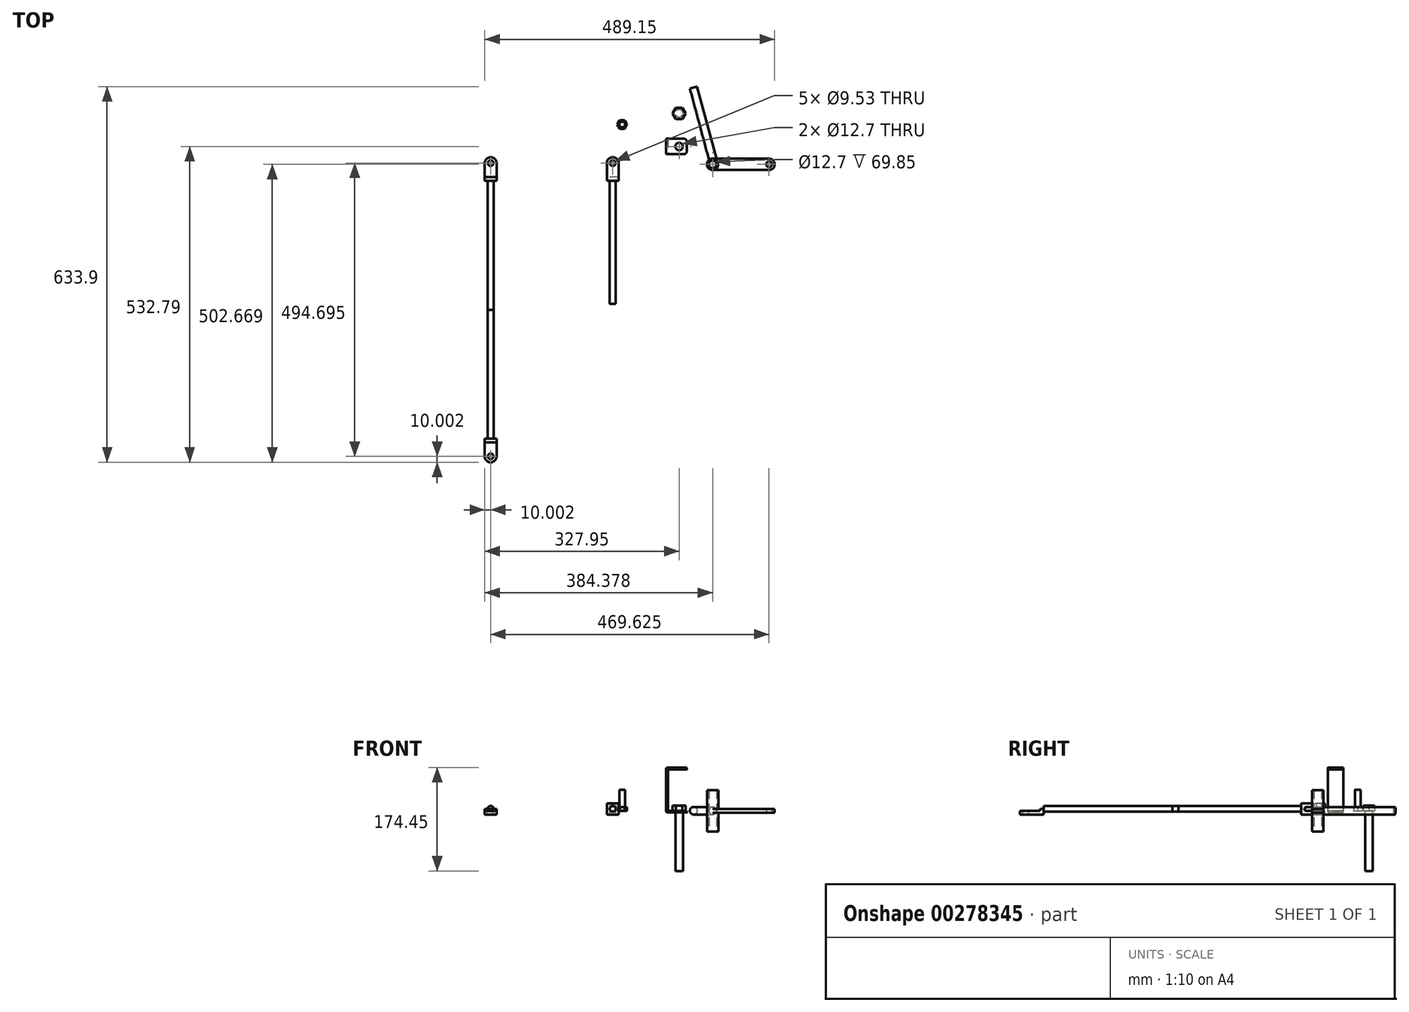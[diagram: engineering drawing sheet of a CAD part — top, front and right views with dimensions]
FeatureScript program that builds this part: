
annotation { "Feature Type Name" : "Feature", "Feature Type Description" : "" }
export const myFeature = defineFeature(function(context is Context, id is Id, definition is map)
    precondition{}
    {
        {
            var Q0;
            Q0=qCreatedBy(makeId("Top.planeOp"),FACE);
            var sketch = newSketch(context, id + "F0", { "sketchPlane" : qUnion([Q0])});
            skCircle(sketch, "E0", {"center": v(0, 0) * mm, "radius": 6.35 * mm});
            skLineSegment(sketch, "E1.bottom", {"start": v(8, 13) * mm, "end": v(-22, 13) * mm});
            skLineSegment(sketch, "E1.top", {"start": v(8, -13) * mm, "end": v(-22, -13) * mm});
            skLineSegment(sketch, "E1.left", {"start": v(13, 8) * mm, "end": v(13, -8) * mm});
            skLineSegment(sketch, "E1.right", {"start": v(-22, 13) * mm, "end": v(-22, -13) * mm});
            skLineSegment(sketch, "E2", {"start": v(-19, 13) * mm, "end": v(-19, -13) * mm});
            skPoint(sketch, "E3.visualSharp", {"position": v(13, 13) * mm});
            skArc(sketch, "E3.filletArc", {"start": v(13, 8) * mm, "mid": v(11.54, 11.54) * mm, "end": v(8, 13) * mm});
            skPoint(sketch, "E4.visualSharp", {"position": v(13, -13) * mm});
            skArc(sketch, "E4.filletArc", {"start": v(8, -13) * mm, "mid": v(11.54, -11.54) * mm, "end": v(13, -8) * mm});
            skSolve(sketch);
        }
        {
            var Q0;
            Q0=makeQuery(id+"F0.imprint","IMPRINT",FACE,{"disambiguationData":[TD([[makeQuery(id+"F0.imprint","IMPRINT",EDGE,{"derivedFrom":sQuery(id+"F0.wireOp",EDGE,"E0")}),-1.0]])]});
            var Q1;
            {var subQ0=sQuery(id+"F0.wireOp",EDGE,"E1.right");Q1=makeQuery(id+"F0.imprint","IMPRINT",FACE,{"disambiguationData":[TD([[makeQuery(id+"F0.imprint","IMPRINT",EDGE,{"derivedFrom":subQ0}),1.0]])]});}
            extrude(context, id + "F1", {"entities" : qUnion([Q0, Q1]), "oppositeDirection" : true, "depth" : 3 * mm});
        }
        {
            var Q0;
            {var subQ0=sQuery(id+"F0.wireOp",EDGE,"E1.right");Q0=makeQuery(id+"F0.imprint","IMPRINT",FACE,{"disambiguationData":[TD([[makeQuery(id+"F0.imprint","IMPRINT",EDGE,{"derivedFrom":subQ0}),1.0]])]});}
            extrude(context, id + "F2", {"entities" : qUnion([Q0]), "operationType" : NewBodyOperationType.ADD, "depth" : 34.92 * mm});
        }
        {
            var Q0;
            Q0=makeQuery(id+"F1.opExtrude","SWEPT_BODY",BODY,{"disambiguationData":[OSD([sQuery(id+"F0.wireOp",EDGE,"E0"),sQuery(id+"F0.wireOp",EDGE,"E1.bottom"),sQuery(id+"F0.wireOp",EDGE,"E1.top"),sQuery(id+"F0.wireOp",EDGE,"E1.left"),sQuery(id+"F0.wireOp",EDGE,"E1.right")])]});
            var Q1;
            Q1=makeQuery(id+"F2.opExtrude","CAP_FACE",FACE,{"disambiguationData":[OSD([sQuery(id+"F0.wireOp",EDGE,"E1.bottom"),sQuery(id+"F0.wireOp",EDGE,"E1.top"),sQuery(id+"F0.wireOp",EDGE,"E1.right"),sQuery(id+"F0.wireOp",EDGE,"E2")])],"isStart":false});
            mirror(context, id + "F3", {"operationType" : NewBodyOperationType.ADD, "entities" : qUnion([Q0]), "mirrorPlane" : qUnion([Q1])});
        }
        {
            var Q0;
            Q0=qCreatedBy(makeId("Top.planeOp"),FACE);
            var sketch = newSketch(context, id + "F4", { "sketchPlane" : qUnion([Q0])});
            skCircle(sketch, "E5.cCircle", {"center": v(0, 56.05) * mm, "radius": 9.53 * mm, "construction": true});
            skLineSegment(sketch, "E5.0", {"start": v(-5.5, 65.57) * mm, "end": v(5.5, 65.57) * mm});
            skLineSegment(sketch, "E5.1", {"start": v(5.5, 65.57) * mm, "end": v(11, 56.05) * mm});
            skLineSegment(sketch, "E5.2", {"start": v(11, 56.05) * mm, "end": v(5.5, 46.52) * mm});
            skLineSegment(sketch, "E5.3", {"start": v(5.5, 46.52) * mm, "end": v(-5.5, 46.52) * mm});
            skLineSegment(sketch, "E5.4", {"start": v(-5.5, 46.52) * mm, "end": v(-11, 56.05) * mm});
            skLineSegment(sketch, "E5.5", {"start": v(-11, 56.05) * mm, "end": v(-5.5, 65.57) * mm});
            skPoint(sketch, "E5.0.midPoint", {"position": v(0, 65.57) * mm});
            skSolve(sketch);
        }
        {
            var Q0;
            Q0=makeQuery(id+"F4.imprint","IMPRINT",FACE,{"disambiguationData":[TD([[makeQuery(id+"F4.imprint","IMPRINT",EDGE,{"derivedFrom":sQuery(id+"F4.wireOp",EDGE,"E5.0")}),-1.0]])]});
            extrude(context, id + "F5", {"entities" : qUnion([Q0]), "depth" : 8.73 * mm});
        }
        {
            var Q0;
            Q0=makeQuery(id+"F5.opExtrude","CAP_FACE",FACE,{"disambiguationData":[OSD([sQuery(id+"F4.wireOp",EDGE,"E5.0"),sQuery(id+"F4.wireOp",EDGE,"E5.1"),sQuery(id+"F4.wireOp",EDGE,"E5.2"),sQuery(id+"F4.wireOp",EDGE,"E5.3"),sQuery(id+"F4.wireOp",EDGE,"E5.4"),sQuery(id+"F4.wireOp",EDGE,"E5.5")])],"isStart":true});
            var sketch = newSketch(context, id + "F6", { "sketchPlane" : qUnion([Q0])});
            skLineSegment(sketch, "E6", {"start": v(11, -56.05) * mm, "end": v(-11, -56.05) * mm, "construction": true});
            skLineSegment(sketch, "E7", {"start": v(0, -65.57) * mm, "end": v(0, -46.52) * mm, "construction": true});
            skCircle(sketch, "E8", {"center": v(0, -56.05) * mm, "radius": 6.35 * mm});
            skSolve(sketch);
        }
        {
            var Q0;
            Q0=makeQuery(id+"F6.imprint","IMPRINT",FACE,{"disambiguationData":[TD([[makeQuery(id+"F6.imprint","IMPRINT",EDGE,{"derivedFrom":sQuery(id+"F6.wireOp",EDGE,"E8")}),1.0]])]});
            extrude(context, id + "F7", {"entities" : qUnion([Q0]), "operationType" : NewBodyOperationType.ADD, "depth" : 101.6 * mm});
        }
        {
            var Q0;
            Q0=qCreatedBy(makeId("Top.planeOp"),FACE);
            var sketch = newSketch(context, id + "F8", { "sketchPlane" : qUnion([Q0])});
            skCircle(sketch, "E9", {"center": v(56.43, -30.12) * mm, "radius": 6.35 * mm});
            skCircle(sketch, "E10", {"center": v(56.43, -30.12) * mm, "radius": 9.53 * mm});
            skLineSegment(sketch, "E11", {"start": v(161.2, -30.12) * mm, "end": v(161.2, -30.12) * mm});
            skLineSegment(sketch, "E12", {"start": v(56.43, -20.6) * mm, "end": v(56.43, -39.65) * mm, "construction": true});
            skLineSegment(sketch, "E13", {"start": v(151.68, -20.6) * mm, "end": v(56.43, -20.6) * mm});
            skLineSegment(sketch, "E14", {"start": v(56.43, -39.65) * mm, "end": v(151.68, -39.65) * mm});
            skLineSegment(sketch, "E15", {"start": v(161.2, -30.12) * mm, "end": v(56.43, -30.12) * mm, "construction": true});
            skPoint(sketch, "E16.visualSharp", {"position": v(161.2, -20.6) * mm});
            skArc(sketch, "E16.filletArc", {"start": v(161.2, -30.12) * mm, "mid": v(158.41, -23.39) * mm, "end": v(151.68, -20.6) * mm});
            skPoint(sketch, "E17.visualSharp", {"position": v(161.2, -39.65) * mm});
            skArc(sketch, "E17.filletArc", {"start": v(151.68, -39.65) * mm, "mid": v(158.41, -36.86) * mm, "end": v(161.2, -30.12) * mm});
            skCircle(sketch, "E18", {"center": v(151.68, -30.12) * mm, "radius": 4.76 * mm});
            skLineSegment(sketch, "E19", {"start": v(56.43, -20.6) * mm, "end": v(24.26, 99.47) * mm, "construction": true});
            skLineSegment(sketch, "E20", {"start": v(24.26, 99.47) * mm, "end": v(18.12, 97.83) * mm});
            skLineSegment(sketch, "E21", {"start": v(24.26, 99.47) * mm, "end": v(30.4, 101.11) * mm});
            skLineSegment(sketch, "E22", {"start": v(30.4, 101.11) * mm, "end": v(63, -20.6) * mm});
            skLineSegment(sketch, "E23", {"start": v(18.12, 97.83) * mm, "end": v(50.42, -22.73) * mm});
            skSolve(sketch);
        }
        {
            var Q0;
            Q0=makeQuery(id+"F8.imprint","IMPRINT",FACE,{"disambiguationData":[TD([[makeQuery(id+"F8.imprint","IMPRINT",EDGE,{"derivedFrom":sQuery(id+"F8.wireOp",EDGE,"E9")}),-1.0]])]});
            extrude(context, id + "F9", {"entities" : qUnion([Q0]), "endBound" : BoundingType.SYMMETRIC, "depth" : 69.85 * mm});
        }
        {
            var Q0;
            Q0=makeQuery(id+"F3.opPattern","COPY",EDGE,{"derivedFrom":makeQuery(id+"F1.opExtrude","CAP_EDGE",EDGE,{"disambiguationData":[OSD([sQuery(id+"F0.wireOp",EDGE,"E1.right")])],"isStart":false}),"instanceName":"1"});
            var Q1;
            Q1=makeQuery(id+"F1.opExtrude","CAP_EDGE",EDGE,{"disambiguationData":[OSD([sQuery(id+"F0.wireOp",EDGE,"E1.right")])],"isStart":false});
            fillet(context, id + "F10", {"entities" : qUnion([Q0, Q1]), "radius" : 2.5 * mm, "tangentPropagation" : true, "allowEdgeOverflow" : false});
        }
        {
            var Q0;
            {var subQ1=sQuery(id+"F8.wireOp",EDGE,"E13");Q0=makeQuery(id+"F8.imprint","IMPRINT",FACE,{"disambiguationData":[TD([[makeQuery(id+"F8.imprint","IMPRINT",EDGE,{"derivedFrom":subQ1}),1.0]])]});}
            extrude(context, id + "F11", {"entities" : qUnion([Q0]), "operationType" : NewBodyOperationType.ADD, "endBound" : BoundingType.SYMMETRIC, "depth" : 6.35 * mm});
        }
        {
            var Q0;
            Q0=makeQuery(id+"F8.imprint","IMPRINT",FACE,{"disambiguationData":[TD([[makeQuery(id+"F8.imprint","IMPRINT",EDGE,{"derivedFrom":sQuery(id+"F8.wireOp",EDGE,"E20")}),1.0]])]});
            extrude(context, id + "F12", {"entities" : qUnion([Q0]), "operationType" : NewBodyOperationType.ADD, "endBound" : BoundingType.SYMMETRIC, "depth" : 12.7 * mm});
        }
        {
            var Q0;
            Q0=makeQuery(id+"F12.opExtrude","CAP_EDGE",EDGE,{"disambiguationData":[OSD([sQuery(id+"F8.wireOp",EDGE,"E22")])],"isStart":false});
            var Q1;
            Q1=makeQuery(id+"F12.opExtrude","CAP_EDGE",EDGE,{"disambiguationData":[OSD([sQuery(id+"F8.wireOp",EDGE,"E23")])],"isStart":false});
            var Q2;
            Q2=makeQuery(id+"F12.opExtrude","CAP_EDGE",EDGE,{"disambiguationData":[OSD([sQuery(id+"F8.wireOp",EDGE,"E22")])],"isStart":true});
            var Q3;
            Q3=makeQuery(id+"F12.opExtrude","CAP_EDGE",EDGE,{"disambiguationData":[OSD([sQuery(id+"F8.wireOp",EDGE,"E23")])],"isStart":true});
            fillet(context, id + "F13", {"entities" : qUnion([Q0, Q1, Q2, Q3]), "radius" : (12.7 / 2) * mm, "tangentPropagation" : true, "allowEdgeOverflow" : false});
        }
        {
            var Q0;
            Q0=qCreatedBy(makeId("Top.planeOp"),FACE);
            var sketch = newSketch(context, id + "F14", { "sketchPlane" : qUnion([Q0])});
            skLineSegment(sketch, "E24.bottom", {"start": v(-101.95, -58.1) * mm, "end": v(-121.95, -58.1) * mm});
            skLineSegment(sketch, "E24.top", {"start": v(-111.95, -18.1) * mm, "end": v(-111.95, -18.1) * mm});
            skLineSegment(sketch, "E24.left", {"start": v(-101.95, -58.1) * mm, "end": v(-101.95, -28.1) * mm});
            skLineSegment(sketch, "E24.right", {"start": v(-121.95, -58.1) * mm, "end": v(-121.95, -28.1) * mm});
            skLineSegment(sketch, "E25", {"start": v(-111.95, -18.1) * mm, "end": v(-111.95, -58.1) * mm, "construction": true});
            skCircle(sketch, "E26", {"center": v(-111.95, -28.1) * mm, "radius": 4.76 * mm});
            skLineSegment(sketch, "E27", {"start": v(-101.95, -51.74) * mm, "end": v(-121.95, -51.74) * mm});
            skPoint(sketch, "E28.visualSharp", {"position": v(-101.95, -18.1) * mm});
            skArc(sketch, "E28.filletArc", {"start": v(-101.95, -28.1) * mm, "mid": v(-104.88, -21.02) * mm, "end": v(-111.95, -18.1) * mm});
            skPoint(sketch, "E29.visualSharp", {"position": v(-121.95, -18.1) * mm});
            skArc(sketch, "E29.filletArc", {"start": v(-111.95, -18.1) * mm, "mid": v(-119.02, -21.02) * mm, "end": v(-121.95, -28.1) * mm});
            skSolve(sketch);
        }
        {
            var Q0;
            Q0=makeQuery(id+"F14.imprint","IMPRINT",FACE,{"disambiguationData":[TD([[makeQuery(id+"F14.imprint","IMPRINT",EDGE,{"derivedFrom":sQuery(id+"F14.wireOp",EDGE,"E26")}),-1.0]])]});
            var Q1;
            {var subQ0=sQuery(id+"F14.wireOp",EDGE,"E24.bottom");Q1=makeQuery(id+"F14.imprint","IMPRINT",FACE,{"disambiguationData":[TD([[makeQuery(id+"F14.imprint","IMPRINT",EDGE,{"derivedFrom":subQ0}),-1.0]])]});}
            extrude(context, id + "F15", {"entities" : qUnion([Q0, Q1]), "oppositeDirection" : true, "depth" : 6.35 * mm});
        }
        {
            var Q0;
            {var subQ0=sQuery(id+"F14.wireOp",EDGE,"E24.bottom");Q0=makeQuery(id+"F14.imprint","IMPRINT",FACE,{"disambiguationData":[TD([[makeQuery(id+"F14.imprint","IMPRINT",EDGE,{"derivedFrom":subQ0}),-1.0]])]});}
            extrude(context, id + "F16", {"entities" : qUnion([Q0]), "operationType" : NewBodyOperationType.ADD, "depth" : (6.35 / 2) * mm});
        }
        {
            var Q0;
            Q0=makeQuery(id+"F15.opExtrude","SWEPT_BODY",BODY,{"disambiguationData":[OSD([sQuery(id+"F14.wireOp",EDGE,"E24.bottom"),sQuery(id+"F14.wireOp",EDGE,"E24.left"),sQuery(id+"F14.wireOp",EDGE,"E24.right"),sQuery(id+"F14.wireOp",EDGE,"E26"),sQuery(id+"F14.wireOp",EDGE,"E28.filletArc"),sQuery(id+"F14.wireOp",EDGE,"E29.filletArc")])]});
            var Q1;
            Q1=makeQuery(id+"F16.opExtrude","CAP_FACE",FACE,{"disambiguationData":[OSD([sQuery(id+"F14.wireOp",EDGE,"E24.bottom"),sQuery(id+"F14.wireOp",EDGE,"E24.left"),sQuery(id+"F14.wireOp",EDGE,"E24.right"),sQuery(id+"F14.wireOp",EDGE,"E27")])],"isStart":false});
            mirror(context, id + "F17", {"operationType" : NewBodyOperationType.ADD, "entities" : qUnion([Q0]), "mirrorPlane" : qUnion([Q1])});
        }
        {
            var Q0;
            Q0=qCreatedBy(makeId("Top.planeOp"),FACE);
            var sketch = newSketch(context, id + "F18", { "sketchPlane" : qUnion([Q0])});
            skCircle(sketch, "E30.cCircle", {"center": v(-96.02, 37.14) * mm, "radius": 7.14 * mm, "construction": true});
            skLineSegment(sketch, "E30.0", {"start": v(-100.15, 44.28) * mm, "end": v(-91.9, 44.28) * mm});
            skLineSegment(sketch, "E30.1", {"start": v(-91.9, 44.28) * mm, "end": v(-87.78, 37.14) * mm});
            skLineSegment(sketch, "E30.2", {"start": v(-87.78, 37.14) * mm, "end": v(-91.9, 30) * mm});
            skLineSegment(sketch, "E30.3", {"start": v(-91.9, 30) * mm, "end": v(-100.15, 30) * mm});
            skLineSegment(sketch, "E30.4", {"start": v(-100.15, 30) * mm, "end": v(-104.27, 37.14) * mm});
            skLineSegment(sketch, "E30.5", {"start": v(-104.27, 37.14) * mm, "end": v(-100.15, 44.28) * mm});
            skPoint(sketch, "E30.0.midPoint", {"position": v(-96.02, 44.28) * mm});
            skCircle(sketch, "E31", {"center": v(-96.02, 37.14) * mm, "radius": 4.76 * mm});
            skSolve(sketch);
        }
        {
            var Q0;
            Q0=makeQuery(id+"F18.imprint","IMPRINT",FACE,{"disambiguationData":[TD([[makeQuery(id+"F18.imprint","IMPRINT",EDGE,{"derivedFrom":sQuery(id+"F18.wireOp",EDGE,"E30.0")}),-1.0]])]});
            var Q1;
            Q1=makeQuery(id+"F18.imprint","IMPRINT",FACE,{"disambiguationData":[TD([[makeQuery(id+"F18.imprint","IMPRINT",EDGE,{"derivedFrom":sQuery(id+"F18.wireOp",EDGE,"E31")}),1.0]])]});
            extrude(context, id + "F19", {"entities" : qUnion([Q0, Q1]), "depth" : 6.35 * mm});
        }
        {
            var Q0;
            Q0=makeQuery(id+"F18.imprint","IMPRINT",FACE,{"disambiguationData":[TD([[makeQuery(id+"F18.imprint","IMPRINT",EDGE,{"derivedFrom":sQuery(id+"F18.wireOp",EDGE,"E31")}),1.0]])]});
            extrude(context, id + "F20", {"entities" : qUnion([Q0]), "operationType" : NewBodyOperationType.ADD, "depth" : 35 * mm});
        }
        {
            var Q0;
            Q0=makeQuery(id+"F15.opExtrude","SWEPT_BODY",BODY,{"disambiguationData":[OSD([sQuery(id+"F14.wireOp",EDGE,"E24.bottom"),sQuery(id+"F14.wireOp",EDGE,"E24.left"),sQuery(id+"F14.wireOp",EDGE,"E24.right"),sQuery(id+"F14.wireOp",EDGE,"E26"),sQuery(id+"F14.wireOp",EDGE,"E28.filletArc"),sQuery(id+"F14.wireOp",EDGE,"E29.filletArc")])]});
            transform(context, id + "F21", {"entities" : qUnion([Q0]), "transformType" : TransformType.TRANSLATION_3D, "dx" : -206 * mm, "dy" : 0 * mm, "dz" : 0 * mm, "makeCopy" : true});
        }
        {
            var Q0;
            {var subQ0=sQuery(id+"F14.wireOp",EDGE,"E24.bottom");var subQ1=makeQuery(id+"F16.boolean.opBoolean","MERGE",FACE,{"derivedFrom":[makeQuery(id+"F15.opExtrude","SWEPT_FACE",FACE,{"disambiguationData":[OSD([subQ0])]}),makeQuery(id+"F16.opExtrude","SWEPT_FACE",FACE,{"disambiguationData":[OSD([subQ0])]})]});Q0=makeQuery(id+"F21.opPattern","COPY",FACE,{"derivedFrom":makeQuery(id+"F17.boolean.opBoolean","MERGE",FACE,{"derivedFrom":[subQ1,makeQuery(id+"F17.opPattern","COPY",FACE,{"derivedFrom":subQ1,"instanceName":"1"})]}),"instanceName":"1"});}
            var sketch = newSketch(context, id + "F22", { "sketchPlane" : qUnion([Q0])});
            skLineSegment(sketch, "E32", {"start": v(-307.95, 12.7) * mm, "end": v(-327.95, -6.35) * mm, "construction": true});
            skLineSegment(sketch, "E33", {"start": v(-327.95, 12.7) * mm, "end": v(-307.95, -6.35) * mm, "construction": true});
            skCircle(sketch, "E34", {"center": v(-317.95, 3.18) * mm, "radius": 5 * mm});
            skSolve(sketch);
        }
        {
            var Q0;
            Q0 = qSketchRegion(id + "F22", true);
            extrude(context, id + "F23", {"entities" : qUnion([Q0]), "operationType" : NewBodyOperationType.ADD, "depth" : (434.7 / 2) * mm});
        }
        {
            var Q0;
            Q0=makeQuery(id+"F21.opPattern","COPY",BODY,{"derivedFrom":makeQuery(id+"F15.opExtrude","SWEPT_BODY",BODY,{"disambiguationData":[OSD([sQuery(id+"F14.wireOp",EDGE,"E24.bottom"),sQuery(id+"F14.wireOp",EDGE,"E24.left"),sQuery(id+"F14.wireOp",EDGE,"E24.right"),sQuery(id+"F14.wireOp",EDGE,"E26"),sQuery(id+"F14.wireOp",EDGE,"E28.filletArc"),sQuery(id+"F14.wireOp",EDGE,"E29.filletArc")])]}),"instanceName":"1"});
            var Q1;
            Q1=makeQuery(id+"F23.opExtrude","CAP_FACE",FACE,{"disambiguationData":[OSD([sQuery(id+"F22.wireOp",EDGE,"E34")])],"isStart":false});
            mirror(context, id + "F24", {"operationType" : NewBodyOperationType.ADD, "entities" : qUnion([Q0]), "mirrorPlane" : qUnion([Q1])});
        }
        {
            var Q0;
            {var subQ0=sQuery(id+"F14.wireOp",EDGE,"E24.bottom");var subQ1=makeQuery(id+"F16.boolean.opBoolean","MERGE",FACE,{"derivedFrom":[makeQuery(id+"F15.opExtrude","SWEPT_FACE",FACE,{"disambiguationData":[OSD([subQ0])]}),makeQuery(id+"F16.opExtrude","SWEPT_FACE",FACE,{"disambiguationData":[OSD([subQ0])]})]});Q0=makeQuery(id+"F17.boolean.opBoolean","MERGE",FACE,{"derivedFrom":[subQ1,makeQuery(id+"F17.opPattern","COPY",FACE,{"derivedFrom":subQ1,"instanceName":"1"})]});}
            var sketch = newSketch(context, id + "F25", { "sketchPlane" : qUnion([Q0])});
            skLineSegment(sketch, "E35", {"start": v(-101.95, 12.7) * mm, "end": v(-121.95, -6.35) * mm, "construction": true});
            skLineSegment(sketch, "E36", {"start": v(-101.95, -6.35) * mm, "end": v(-121.95, 12.7) * mm, "construction": true});
            skCircle(sketch, "E37", {"center": v(-111.95, 3.18) * mm, "radius": 5 * mm});
            skSolve(sketch);
        }
        {
            var Q0;
            Q0=makeQuery(id+"F25.imprint","IMPRINT",FACE,{"disambiguationData":[TD([[makeQuery(id+"F25.imprint","IMPRINT",EDGE,{"derivedFrom":sQuery(id+"F25.wireOp",EDGE,"E37")}),1.0]])]});
            extrude(context, id + "F26", {"entities" : qUnion([Q0]), "operationType" : NewBodyOperationType.ADD, "depth" : 207.35 * mm});
        }
    });
